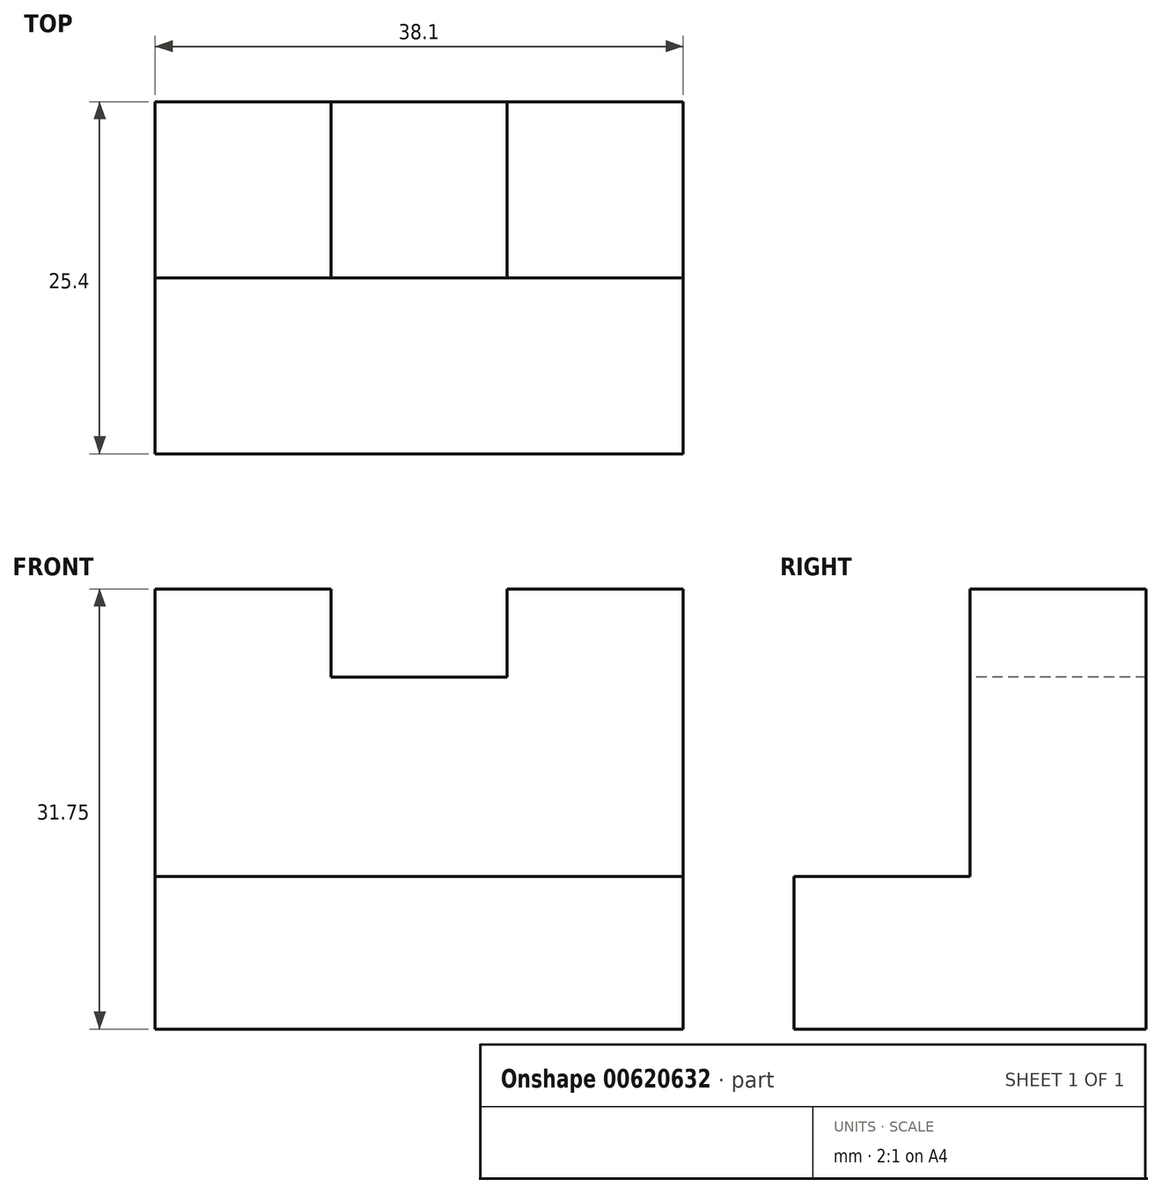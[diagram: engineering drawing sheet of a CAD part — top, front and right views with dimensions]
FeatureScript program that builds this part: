
annotation { "Feature Type Name" : "Feature", "Feature Type Description" : "" }
export const myFeature = defineFeature(function(context is Context, id is Id, definition is map)
    precondition{}
    {
        {
            var Q0;
            Q0=qCreatedBy(makeId("Front.planeOp"),FACE);
            var sketch = newSketch(context, id + "F0", { "sketchPlane" : qUnion([Q0])});
            skLineSegment(sketch, "E0", {"start": v(0, 0) * mm, "end": v(38.1, 0) * mm});
            skLineSegment(sketch, "E1", {"start": v(38.1, 0) * mm, "end": v(38.1, 31.75) * mm});
            skLineSegment(sketch, "E2", {"start": v(38.1, 31.75) * mm, "end": v(0, 31.75) * mm});
            skLineSegment(sketch, "E3", {"start": v(0, 31.75) * mm, "end": v(0, 0) * mm});
            skSolve(sketch);
        }
        {
            var Q0;
            Q0=makeQuery(id+"F0.imprint","IMPRINT",FACE,{"disambiguationData":[TD([[makeQuery(id+"F0.imprint","IMPRINT",EDGE,{"derivedFrom":sQuery(id+"F0.wireOp",EDGE,"E0")}),1.0]])]});
            extrude(context, id + "F1", {"entities" : qUnion([Q0]), "depth" : 25.4 * mm, "offsetDistance" : 25.4 * mm});
        }
        {
            var Q0;
            Q0=makeQuery(id+"F1.opExtrude","CAP_FACE",FACE,{"disambiguationData":[OSD([sQuery(id+"F0.wireOp",EDGE,"E0"),sQuery(id+"F0.wireOp",EDGE,"E1"),sQuery(id+"F0.wireOp",EDGE,"E2"),sQuery(id+"F0.wireOp",EDGE,"E3")])],"isStart":false});
            var sketch = newSketch(context, id + "F2", { "sketchPlane" : qUnion([Q0])});
            skLineSegment(sketch, "E4", {"start": v(38.1, 11) * mm, "end": v(0, 11) * mm});
            skPoint(sketch, "E4.endSnap0", {"position": v(0, 15.88) * mm});
            skSolve(sketch);
        }
        {
            var Q0;
            {var subQ0=sQuery(id+"F2.wireOp",EDGE,"E4");Q0=makeQuery(id+"F2.imprint","IMPRINT",FACE,{"disambiguationData":[TD([[makeQuery(id+"F2.imprint","IMPRINT",EDGE,{"derivedFrom":subQ0}),-1.0]])]});}
            extrude(context, id + "F3", {"entities" : qUnion([Q0]), "operationType" : NewBodyOperationType.REMOVE, "oppositeDirection" : true, "depth" : 12.7 * mm, "offsetDistance" : 25.4 * mm});
        }
        {
            var Q0;
            Q0=makeQuery(id+"F1.opExtrude","SWEPT_FACE",FACE,{"disambiguationData":[OSD([sQuery(id+"F0.wireOp",EDGE,"E2")])]});
            var sketch = newSketch(context, id + "F4", { "sketchPlane" : qUnion([Q0])});
            skLineSegment(sketch, "E5", {"start": v(0, 0) * mm, "end": v(12.7, 0) * mm});
            skLineSegment(sketch, "E6", {"start": v(12.7, 0) * mm, "end": v(12.7, -12.7) * mm});
            skLineSegment(sketch, "E7", {"start": v(0, 0) * mm, "end": v(0, -12.7) * mm});
            skLineSegment(sketch, "E8", {"start": v(0, -12.7) * mm, "end": v(12.7, -12.7) * mm});
            skLineSegment(sketch, "E9", {"start": v(38.1, 0) * mm, "end": v(25.4, 0) * mm});
            skLineSegment(sketch, "E10", {"start": v(25.4, 0) * mm, "end": v(25.4, -12.7) * mm});
            skLineSegment(sketch, "E11", {"start": v(25.4, -12.7) * mm, "end": v(38.1, -12.7) * mm});
            skLineSegment(sketch, "E12", {"start": v(38.1, -12.7) * mm, "end": v(38.1, -6.35) * mm});
            skLineSegment(sketch, "E13", {"start": v(38.1, -12.7) * mm, "end": v(38.1, 0) * mm});
            skLineSegment(sketch, "E14", {"start": v(25.4, -12.7) * mm, "end": v(12.7, -12.7) * mm});
            skLineSegment(sketch, "E15", {"start": v(25.4, 0) * mm, "end": v(12.7, 0) * mm});
            skLineSegment(sketch, "E16", {"start": v(12.7, -12.7) * mm, "end": v(25.4, -12.7) * mm});
            skLineSegment(sketch, "E17", {"start": v(25.4, -12.7) * mm, "end": v(25.4, 0) * mm});
            skSolve(sketch);
        }
        {
            var Q0;
            Q0=makeQuery(id+"F4.imprint","IMPRINT",FACE,{"disambiguationData":[TD([[makeQuery(id+"F4.imprint","IMPRINT",EDGE,{"derivedFrom":sQuery(id+"F4.wireOp",EDGE,"E15")}),1.0]])]});
            extrude(context, id + "F5", {"entities" : qUnion([Q0]), "operationType" : NewBodyOperationType.REMOVE, "oppositeDirection" : true, "depth" : 6.35 * mm, "offsetDistance" : 25.4 * mm});
        }
    });
